# Revit family: BG-0600 - Floor-Floor
name_source: partatom
category: Specialty Equipment
units: mm (PartAtom-declared; Revit-internal decimal feet)

## family parameters
Cut with Voids When Loaded = No
Host = Face
Part Type = Normal
Room Calculation Point = No
Round Connector Dimension = Use Diameter
Shared = No

## types (1)
- SEE TYPE CATEGORY
    Assembly Code = C3020200
    Default Elevation = 0"
    Depth = 1 15/16"
    Description = RoofJoint is a patented dual-seal, double-flanged, extruded thermoplastic rubber system for sealing positive-side below-grade wall, blind-side formed foundation walls, and under slabs
    Manufacturer = EMSEAL Joint Systems Ltd
    Manufacturer URL = http://www.emseal.com
    Model = BG-0600
    Movement (of Nominal Material Size) = +50% / -50%
    Product Documentataion URL = https://bit.ly
    Product Page URL = https://bit.ly
    Seal Material = Rubber, Nitrile - Plasticized NPVC - Black
    Top Flap Width = 1' - 5 1/4"
    Type Image = <None>
    Weldable = Yes
    Width = 6"

## geometry (parser evidence)
native form markers: Sweep x2
no freeform markers — native parametric forms only
